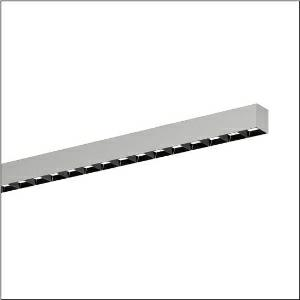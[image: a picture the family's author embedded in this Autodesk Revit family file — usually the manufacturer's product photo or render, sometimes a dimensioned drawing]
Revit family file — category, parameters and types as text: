
# Revit family: silica_21_51mx24tat4s
name_source: partatom
category: Lighting Fixtures
units: mm (PartAtom-declared; Revit-internal decimal feet)

## family parameters
Cut with Voids When Loaded = No
Host = Face
Light Source = No
Part Type = Normal
Room Calculation Point = No
Round Connector Dimension = Use Diameter
Shared = No

## types (1)
- --- (1 x LED, 3280 lm, 32.4 W, 6500K)
    Apparent Load = 32 VA
    CIE Flux Codes = 74 94 99 100 100
    Color Rendering = 80
    Color Temperature = 6500K
    Default Elevation = 1800 mm
    Description = Silica 21, office luminaire, primary light control with darklight reflector, of PMMA, black, light emission: direct distribution, primary light characteristic: asymmetric, installation type: surface-mounted, LED, rated luminous flux: 3.280lm, luminous efficacy: 96lm/W, light colour: 8tw, colour temperature: 2700..6500K, control gear: DALI DT8, with terminal, 3+2-pole, max. 2.5mm², mains connection: 220..240V, AC, 50/60Hz, rated input power: 34.1W, luminaire housing, of aluminium, metallic grey (RAL 9006), length: 1.204mm, width: 53mm, height: 53mm, protection rating (complete): IP20, insulation class (complete): insulation class I (protective earthing), certification: CE, permissible operating ambient temperature: 0..+35°C, standard: EN 50419, packaging unit: 1 piece
    Height = 53 mm
    Lamp = 1 x LED
    Lamp Light Flux = 3280 lm
    Lamp Power = 32.4 W
    Lamp count = 1
    Length = 1204 mm
    Luminous efficacy = 101 lm/W
    Manufacturer = Siteco
    ModVariant = No
    Model = 51MX24TAT4S
    Mounting Place = Ceiling
    Mounting Type = Surface mounted
    Number of Poles = 1
    OnlyDefault = Yes
    Power Factor = 1
    Product Name = Silica 21
    Product group = office luminaire | ceiling mounted
    ProductGroupID = 301
    Protection Class = Protection class I
    Protection Degree = IP 20
    RLX_Detail_Level = 1
    RLX_Emergency_Light_Flux = 0 lm
    RLX_Emergency_Type = 0
    RLX_Emergency_Type_DB = No
    RlxData = <blob elided: 39669 chars, md5=9ed487fe>
    Socket = socket
    Standby Power = 0 W
    System Light Flux = 3280 lm
    System Power = 32 W
    Type Comments = individual setting
    Type Image = l_1335929.jpg
    URL = http://relux.com
    VarID = @adj_139475
    Voltage = 0 V
    Weight = 0.00 kg
    Width = 53 mm

## geometry (parser evidence)
native form markers: Blend x4, Sweep x9
no freeform markers — native parametric forms only
